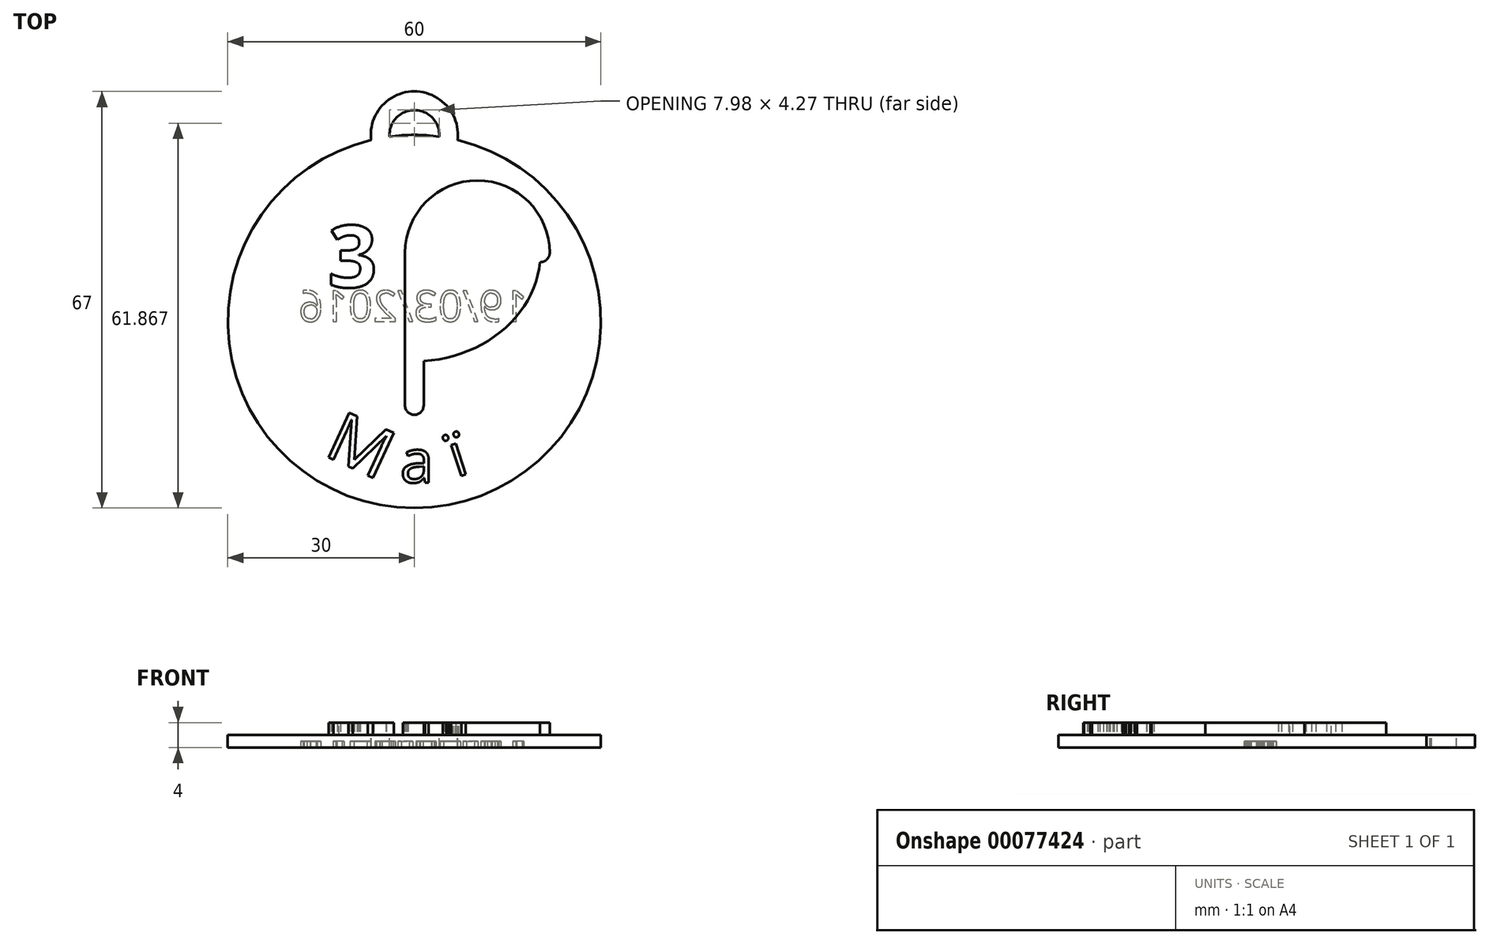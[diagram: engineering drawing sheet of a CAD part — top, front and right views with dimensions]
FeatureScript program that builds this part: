
annotation { "Feature Type Name" : "Feature", "Feature Type Description" : "" }
export const myFeature = defineFeature(function(context is Context, id is Id, definition is map)
    precondition{}
    {
        {
            var Q0;
            Q0=qCreatedBy(makeId("Top.planeOp"),FACE);
            var sketch = newSketch(context, id + "F0", { "sketchPlane" : qUnion([Q0])});
            skCircle(sketch, "E0", {"center": v(0, 0) * mm, "radius": 30 * mm});
            skSolve(sketch);
        }
        {
            var Q0;
            Q0=qSketchRegion(id+"F0",true);
            extrude(context, id + "F1", {"entities" : qUnion([Q0]), "oppositeDirection" : true, "depth" : 2 * mm});
        }
        {
            var Q0;
            Q0=qCreatedBy(makeId("Top.planeOp"),FACE);
            var sketch = newSketch(context, id + "F2", { "sketchPlane" : qUnion([Q0])});
            skEllipticalArc(sketch, "E1", {});
            skLineSegment(sketch, "E2", {"start": v(0, 0) * mm, "end": v(0, 30) * mm, "construction": true});
            skLineSegment(sketch, "E3", {"start": v(0, 11.04) * mm, "end": v(0, -13.5) * mm});
            skArc(sketch, "E4", {"start": v(20.27, 11.04) * mm, "mid": v(10.13, 21.17) * mm, "end": v(0, 11.04) * mm});
            skLineSegment(sketch, "E5", {"start": v(0, 11.04) * mm, "end": v(-16.84, 20.76) * mm, "construction": true});
            skLineSegment(sketch, "E6", {"start": v(0, 11.04) * mm, "end": v(-20.27, 11.04) * mm, "construction": true});
            skArc(sketch, "E7.0.startCap", {"start": v(-1.5, 11.04) * mm, "mid": v(0, 12.54) * mm, "end": v(1.5, 11.04) * mm});
            skArc(sketch, "E7.0.endCap", {"start": v(1.5, -13.5) * mm, "mid": v(0, -15) * mm, "end": v(-1.5, -13.5) * mm});
            skLineSegment(sketch, "E7.0.left", {"start": v(1.5, 11.04) * mm, "end": v(1.5, -13.5) * mm});
            skLineSegment(sketch, "E7.0.right", {"start": v(-1.5, 11.04) * mm, "end": v(-1.5, -13.5) * mm});
            skArc(sketch, "E8.0.startCap", {"start": v(21.77, 11.04) * mm, "mid": v(20.27, 9.54) * mm, "end": v(18.77, 11.04) * mm});
            skArc(sketch, "E8.0.endCap", {"start": v(1.5, 11.04) * mm, "mid": v(0, 9.54) * mm, "end": v(-1.5, 11.04) * mm});
            skArc(sketch, "E8.0.left", {"start": v(18.77, 11.04) * mm, "mid": v(10.13, 19.67) * mm, "end": v(1.5, 11.04) * mm});
            skArc(sketch, "E8.0.right", {"start": v(21.77, 11.04) * mm, "mid": v(10.13, 22.67) * mm, "end": v(-1.5, 11.04) * mm});
            skArc(sketch, "E8.1.startCap", {"start": v(-18.02, 21.68) * mm, "mid": v(-15.91, 21.95) * mm, "end": v(-15.65, 19.84) * mm});
            skArc(sketch, "E8.1.endCap", {"start": v(18.77, 11.04) * mm, "mid": v(20.27, 12.54) * mm, "end": v(21.77, 11.04) * mm});
            skFitSpline(sketch, "E8.1.left", {"points": [v(18.7, 9.5) * mm, v(18.8, 11.04) * mm, v(18.7, 12.6) * mm, v(18.36, 14.63) * mm, v(17.66, 16.6) * mm, v(16.63, 18.49) * mm, v(15.37, 20.3) * mm, v(13.44, 22.32) * mm, v(11.07, 24) * mm, v(8.94, 25.1) * mm, v(6.7, 26.01) * mm, v(4.32, 26.63) * mm, v(1.87, 26.95) * mm, v(0, 27.03) * mm, v(-1.87, 26.95) * mm, v(-4.32, 26.63) * mm, v(-6.7, 26.01) * mm, v(-8.94, 25.1) * mm, v(-11.07, 24) * mm, v(-13.44, 22.32) * mm, v(-15.37, 20.3) * mm, v(-16.63, 18.49) * mm, v(-17.66, 16.6) * mm, v(-18.36, 14.63) * mm, v(-18.7, 12.6) * mm, v(-18.8, 11.04) * mm, v(-18.7, 9.5) * mm, v(-18.36, 7.46) * mm, v(-17.66, 5.48) * mm, v(-16.63, 3.6) * mm, v(-15.37, 1.8) * mm, v(-13.44, -0.24) * mm, v(-11.07, -1.92) * mm, v(-8.94, -3.02) * mm, v(-6.7, -3.93) * mm, v(-4.32, -4.55) * mm, v(-1.87, -4.86) * mm, v(0, -4.94) * mm, v(1.87, -4.86) * mm, v(4.32, -4.55) * mm, v(6.7, -3.93) * mm, v(8.94, -3.02) * mm, v(11.07, -1.92) * mm, v(13.44, -0.24) * mm, v(15.37, 1.8) * mm, v(16.63, 3.6) * mm, v(17.66, 5.48) * mm, v(18.36, 7.46) * mm, v(18.7, 9.5) * mm, v(18.8, 11.04) * mm, v(18.7, 12.6) * mm]});
            skFitSpline(sketch, "E8.1.right", {"points": [v(21.7, 9.15) * mm, v(21.8, 11.04) * mm, v(21.7, 12.93) * mm, v(21.27, 15.42) * mm, v(20.42, 17.81) * mm, v(19.18, 20.07) * mm, v(17.69, 22.22) * mm, v(15.4, 24.61) * mm, v(12.65, 26.56) * mm, v(10.2, 27.83) * mm, v(7.62, 28.88) * mm, v(4.92, 29.58) * mm, v(2.12, 29.94) * mm, v(0, 30.03) * mm, v(-2.12, 29.94) * mm, v(-4.92, 29.58) * mm, v(-7.62, 28.88) * mm, v(-10.2, 27.83) * mm, v(-12.65, 26.56) * mm, v(-15.4, 24.61) * mm, v(-17.69, 22.22) * mm, v(-19.18, 20.07) * mm, v(-20.42, 17.81) * mm, v(-21.27, 15.42) * mm, v(-21.7, 12.93) * mm, v(-21.8, 11.04) * mm, v(-21.7, 9.15) * mm, v(-21.27, 6.67) * mm, v(-20.42, 4.27) * mm, v(-19.18, 2) * mm, v(-17.69, -0.14) * mm, v(-15.4, -2.53) * mm, v(-12.65, -4.48) * mm, v(-10.2, -5.75) * mm, v(-7.62, -6.8) * mm, v(-4.92, -7.5) * mm, v(-2.12, -7.86) * mm, v(0, -7.95) * mm, v(2.12, -7.86) * mm, v(4.92, -7.5) * mm, v(7.62, -6.8) * mm, v(10.2, -5.75) * mm, v(12.65, -4.48) * mm, v(15.4, -2.53) * mm, v(17.69, -0.14) * mm, v(19.18, 2) * mm, v(20.42, 4.27) * mm, v(21.27, 6.67) * mm, v(21.7, 9.15) * mm, v(21.8, 11.04) * mm, v(21.7, 12.93) * mm]});
            const initialGuessF2  = {"E1": [0, 0.011041626236194823, 1, 0, 0.020266667008310185, 0.017458373763805178, 2.5511335140588507, 0]};
            skSetInitialGuess(sketch, initialGuessF2);
            skSolve(sketch);
        }
        {
            var Q0;
            {var subQ0=sQuery(id+"F2.wireOp",EDGE,"E8.1.startCap");Q0=makeQuery(id+"F2.imprint","IMPRINT",FACE,{"disambiguationData":[TD([[makeQuery(id+"F2.imprint","IMPRINT",EDGE,{"derivedFrom":subQ0}),-1.0]])]});}
            var Q1;
            {var subQ0=sQuery(id+"F2.wireOp",EDGE,"E7.0.right");var subQ1=sQuery(id+"F2.wireOp",EDGE,"E1");var subQ2=makeQuery(id+"F2.imprint","INTERSECT",VERTEX,{"derivedFrom":[subQ1,subQ0]});Q1=makeQuery(id+"F2.imprint","IMPRINT",FACE,{"disambiguationData":[TD([[makeQuery(id+"F2.imprint","IMPRINT",EDGE,{"disambiguationData":[TD([[subQ2,-1.0]])],"derivedFrom":subQ1}),1.0]])]});}
            var Q2;
            {var subQ0=sQuery(id+"F2.wireOp",EDGE,"E3");var subQ1=sQuery(id+"F2.wireOp",EDGE,"E1");var subQ2=makeQuery(id+"F2.imprint","INTERSECT",VERTEX,{"derivedFrom":[subQ1,subQ0]});Q2=makeQuery(id+"F2.imprint","IMPRINT",FACE,{"disambiguationData":[TD([[makeQuery(id+"F2.imprint","IMPRINT",EDGE,{"disambiguationData":[TD([[subQ2,-1.0]])],"derivedFrom":subQ1}),1.0]])]});}
            var Q3;
            {var subQ0=sQuery(id+"F2.wireOp",EDGE,"E7.0.right");var subQ1=sQuery(id+"F2.wireOp",EDGE,"E1");var subQ2=makeQuery(id+"F2.imprint","INTERSECT",VERTEX,{"derivedFrom":[subQ1,subQ0]});Q3=makeQuery(id+"F2.imprint","IMPRINT",FACE,{"disambiguationData":[TD([[makeQuery(id+"F2.imprint","IMPRINT",EDGE,{"disambiguationData":[TD([[subQ2,-1.0]])],"derivedFrom":subQ1}),-1.0]])]});}
            var Q4;
            {var subQ0=sQuery(id+"F2.wireOp",EDGE,"E3");var subQ1=sQuery(id+"F2.wireOp",EDGE,"E1");var subQ2=makeQuery(id+"F2.imprint","INTERSECT",VERTEX,{"derivedFrom":[subQ1,subQ0]});Q4=makeQuery(id+"F2.imprint","IMPRINT",FACE,{"disambiguationData":[TD([[makeQuery(id+"F2.imprint","IMPRINT",EDGE,{"disambiguationData":[TD([[subQ2,-1.0]])],"derivedFrom":subQ1}),-1.0]])]});}
            var Q5;
            {var subQ0=sQuery(id+"F2.wireOp",EDGE,"E7.0.left");var subQ1=sQuery(id+"F2.wireOp",EDGE,"E1");var subQ2=makeQuery(id+"F2.imprint","INTERSECT",VERTEX,{"derivedFrom":[subQ1,subQ0]});Q5=makeQuery(id+"F2.imprint","IMPRINT",FACE,{"disambiguationData":[TD([[makeQuery(id+"F2.imprint","IMPRINT",EDGE,{"disambiguationData":[TD([[subQ2,-1.0]])],"derivedFrom":subQ1}),-1.0]])]});}
            var Q6;
            {var subQ0=sQuery(id+"F2.wireOp",EDGE,"E7.0.left");var subQ1=sQuery(id+"F2.wireOp",EDGE,"E1");var subQ2=makeQuery(id+"F2.imprint","INTERSECT",VERTEX,{"derivedFrom":[subQ1,subQ0]});Q6=makeQuery(id+"F2.imprint","IMPRINT",FACE,{"disambiguationData":[TD([[makeQuery(id+"F2.imprint","IMPRINT",EDGE,{"disambiguationData":[TD([[subQ2,-1.0]])],"derivedFrom":subQ1}),1.0]])]});}
            var Q7;
            {var subQ0=sQuery(id+"F2.wireOp",EDGE,"E4");var subQ1=sQuery(id+"F2.wireOp",EDGE,"E1");var subQ2=makeQuery(id+"F2.imprint","INTERSECT",VERTEX,{"derivedFrom":[subQ1,subQ0]});Q7=makeQuery(id+"F2.imprint","IMPRINT",FACE,{"disambiguationData":[TD([[makeQuery(id+"F2.imprint","IMPRINT",EDGE,{"disambiguationData":[TD([[subQ2,1.0]])],"derivedFrom":subQ1}),-1.0]])]});}
            var Q8;
            {var subQ0=sQuery(id+"F2.wireOp",EDGE,"E4");var subQ1=sQuery(id+"F2.wireOp",EDGE,"E1");var subQ2=makeQuery(id+"F2.imprint","INTERSECT",VERTEX,{"derivedFrom":[subQ1,subQ0]});Q8=makeQuery(id+"F2.imprint","IMPRINT",FACE,{"disambiguationData":[TD([[makeQuery(id+"F2.imprint","IMPRINT",EDGE,{"disambiguationData":[TD([[subQ2,1.0]])],"derivedFrom":subQ1}),1.0]])]});}
            var Q9;
            {var subQ5=sQuery(id+"F2.wireOp",EDGE,"E8.0.left");Q9=makeQuery(id+"F2.imprint","IMPRINT",FACE,{"disambiguationData":[TD([[makeQuery(id+"F2.imprint","IMPRINT",EDGE,{"derivedFrom":subQ5}),-1.0]])]});}
            var Q10;
            {var subQ5=sQuery(id+"F2.wireOp",EDGE,"E8.0.right");Q10=makeQuery(id+"F2.imprint","IMPRINT",FACE,{"disambiguationData":[TD([[makeQuery(id+"F2.imprint","IMPRINT",EDGE,{"derivedFrom":subQ5}),1.0]])]});}
            var Q11;
            {var subQ0=sQuery(id+"F2.wireOp",EDGE,"E4");var subQ1=sQuery(id+"F2.wireOp",EDGE,"E3");var subQ2=makeQuery(id+"F2.imprint","INTERSECT",VERTEX,{"derivedFrom":[subQ1,subQ0]});Q11=makeQuery(id+"F2.imprint","IMPRINT",FACE,{"disambiguationData":[TD([[makeQuery(id+"F2.imprint","IMPRINT",EDGE,{"disambiguationData":[TD([[subQ2,-1.0]])],"derivedFrom":subQ1}),-1.0]])]});}
            var Q12;
            {var subQ0=sQuery(id+"F2.wireOp",EDGE,"E4");var subQ1=sQuery(id+"F2.wireOp",EDGE,"E3");var subQ2=makeQuery(id+"F2.imprint","INTERSECT",VERTEX,{"derivedFrom":[subQ1,subQ0]});Q12=makeQuery(id+"F2.imprint","IMPRINT",FACE,{"disambiguationData":[TD([[makeQuery(id+"F2.imprint","IMPRINT",EDGE,{"disambiguationData":[TD([[subQ2,-1.0]])],"derivedFrom":subQ1}),1.0]])]});}
            var Q13;
            {var subQ0=sQuery(id+"F2.wireOp",EDGE,"E8.0.endCap");var subQ1=sQuery(id+"F2.wireOp",EDGE,"E3");var subQ2=makeQuery(id+"F2.imprint","INTERSECT",VERTEX,{"derivedFrom":[subQ1,subQ0]});Q13=makeQuery(id+"F2.imprint","IMPRINT",FACE,{"disambiguationData":[TD([[makeQuery(id+"F2.imprint","IMPRINT",EDGE,{"disambiguationData":[TD([[subQ2,-1.0]])],"derivedFrom":subQ1}),-1.0]])]});}
            var Q14;
            {var subQ0=sQuery(id+"F2.wireOp",EDGE,"E8.0.endCap");var subQ1=sQuery(id+"F2.wireOp",EDGE,"E3");var subQ2=makeQuery(id+"F2.imprint","INTERSECT",VERTEX,{"derivedFrom":[subQ1,subQ0]});Q14=makeQuery(id+"F2.imprint","IMPRINT",FACE,{"disambiguationData":[TD([[makeQuery(id+"F2.imprint","IMPRINT",EDGE,{"disambiguationData":[TD([[subQ2,-1.0]])],"derivedFrom":subQ1}),1.0]])]});}
            var Q15;
            {var subQ1=sQuery(id+"F2.wireOp",EDGE,"E7.0.endCap");Q15=makeQuery(id+"F2.imprint","IMPRINT",FACE,{"disambiguationData":[TD([[makeQuery(id+"F2.imprint","IMPRINT",EDGE,{"derivedFrom":subQ1}),-1.0]])]});}
            extrude(context, id + "F3", {"entities" : qUnion([Q0, Q1, Q2, Q3, Q4, Q5, Q6, Q7, Q8, Q9, Q10, Q11, Q12, Q13, Q14, Q15]), "operationType" : NewBodyOperationType.ADD, "depth" : 2 * mm});
        }
        {
            var Q0;
            Q0=qCreatedBy(makeId("Top.planeOp"),FACE);
            var sketch = newSketch(context, id + "F4", { "sketchPlane" : qUnion([Q0])});
            skText(sketch, "E9", { "text": "3", "fontName": "OpenSans-Bold.ttf"});
            skText(sketch, "E10", { "text": "D", "fontName": "OpenSans-Bold.ttf"});
            const initialGuessF4  = {"E9": [-0.0139, 0.0055, 1, 0, 0.01], "E10": [0.0055, 0.0055, 1, 0, 0.01]};
            skSetInitialGuess(sketch, initialGuessF4);
            skSolve(sketch);
        }
        {
            var Q0;
            Q0=qSketchRegion(id+"F4",true);
            extrude(context, id + "F5", {"entities" : qUnion([Q0]), "operationType" : NewBodyOperationType.ADD, "depth" : 2 * mm});
        }
        {
            var Q0;
            {var subQ8=sQuery(id+"F0.wireOp",EDGE,"E0");Q0=makeQuery(id+"F3.boolean.opBoolean","SPLIT",FACE,{"disambiguationData":[TD([makeQuery(id+"F1.opExtrude","SWEPT_FACE",FACE,{"disambiguationData":[OSD([subQ8])]})])],"derivedFrom":makeQuery(id+"F1.opExtrude","CAP_FACE",FACE,{"disambiguationData":[OSD([subQ8])],"isStart":true})});}
            var sketch = newSketch(context, id + "F6", { "sketchPlane" : qUnion([Q0])});
            skCircle(sketch, "E11.0", {"center": v(0, 0) * mm, "radius": 26 * mm, "construction": true});
            skText(sketch, "E12", { "text": "M", "fontName": "OpenSans-Regular.ttf"});
            skText(sketch, "E13", { "text": "a", "fontName": "OpenSans-Regular.ttf"});
            skText(sketch, "E14", { "text": "ï", "fontName": "OpenSans-Regular.ttf"});
            const initialGuessF6  = {"E12": [-0.01477, -0.0214, 0.90838, -0.41816, 0.008], "E13": [-0.0023, -0.0259, 1, 0, 0.007], "E14": [0.00674, -0.02511, 0.95123, 0.30848, 0.007]};
            skSetInitialGuess(sketch, initialGuessF6);
            skSolve(sketch);
        }
        {
            var Q0;
            Q0=qSketchRegion(id+"F6",true);
            extrude(context, id + "F7", {"entities" : qUnion([Q0]), "operationType" : NewBodyOperationType.ADD, "depth" : 2 * mm});
        }
        {
            var Q0;
            Q0=qCreatedBy(makeId("Top.planeOp"),FACE);
            var sketch = newSketch(context, id + "F8", { "sketchPlane" : qUnion([Q0])});
            skArc(sketch, "E15", {"start": v(5.48, 29.5) * mm, "mid": v(0, 35.5) * mm, "end": v(-5.48, 29.5) * mm});
            skArc(sketch, "E16.0.startCap", {"start": v(6.97, 29.36) * mm, "mid": v(5.34, 28) * mm, "end": v(3.98, 29.63) * mm});
            skArc(sketch, "E16.0.endCap", {"start": v(-3.98, 29.63) * mm, "mid": v(-5.34, 28) * mm, "end": v(-6.97, 29.36) * mm});
            skArc(sketch, "E16.0.left", {"start": v(3.98, 29.63) * mm, "mid": v(0, 34) * mm, "end": v(-3.98, 29.63) * mm});
            skArc(sketch, "E16.0.right", {"start": v(6.97, 29.36) * mm, "mid": v(0, 37) * mm, "end": v(-6.97, 29.36) * mm});
            skSolve(sketch);
        }
        {
            var Q0;
            Q0=qSketchRegion(id+"F8",true);
            extrude(context, id + "F9", {"entities" : qUnion([Q0]), "operationType" : NewBodyOperationType.ADD, "oppositeDirection" : true, "depth" : 2 * mm});
        }
        {
            var Q0;
            Q0=makeQuery(id+"F9.boolean.opBoolean","MERGE",FACE,{"derivedFrom":[makeQuery(id+"F1.opExtrude","CAP_FACE",FACE,{"disambiguationData":[OSD([sQuery(id+"F0.wireOp",EDGE,"E0")])],"isStart":false}),makeQuery(id+"F9.opExtrude","CAP_FACE",FACE,{"disambiguationData":[OSD([sQuery(id+"F8.wireOp",EDGE,"E16.0.startCap"),sQuery(id+"F8.wireOp",EDGE,"E16.0.endCap"),sQuery(id+"F8.wireOp",EDGE,"E16.0.left"),sQuery(id+"F8.wireOp",EDGE,"E16.0.right")])],"isStart":false})]});
            var sketch = newSketch(context, id + "F10", { "sketchPlane" : qUnion([Q0])});
            skText(sketch, "E17", { "text": "19/03/2016", "fontName": "OpenSans-Regular.ttf"});
            const initialGuessF10  = {"E17": [0.01826, 0, -1, 0, 0.005]};
            skSetInitialGuess(sketch, initialGuessF10);
            skSolve(sketch);
        }
        {
            var Q0;
            Q0=qSketchRegion(id+"F10",true);
            extrude(context, id + "F11", {"entities" : qUnion([Q0]), "operationType" : NewBodyOperationType.REMOVE, "oppositeDirection" : true, "depth" : 1 * mm});
        }
    });
